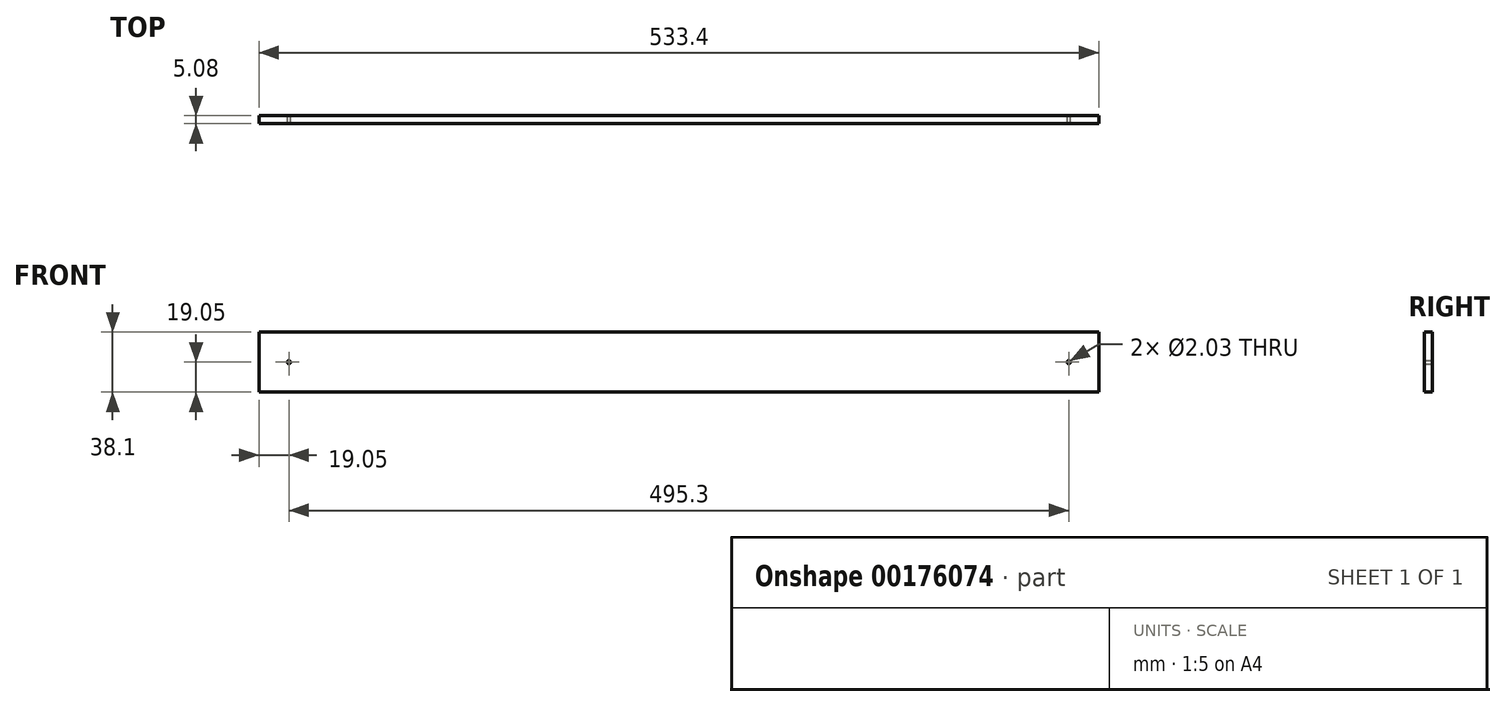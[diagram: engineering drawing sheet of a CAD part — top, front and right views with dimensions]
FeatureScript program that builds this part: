
annotation { "Feature Type Name" : "Feature", "Feature Type Description" : "" }
export const myFeature = defineFeature(function(context is Context, id is Id, definition is map)
    precondition{}
    {
        {
            var Q0;
            Q0=qCreatedBy(makeId("Front.planeOp"),FACE);
            var sketch = newSketch(context, id + "F0", { "sketchPlane" : qUnion([Q0])});
            skLineSegment(sketch, "E0.bottom", {"start": v(0, 0) * mm, "end": v(533.4, 0) * mm});
            skLineSegment(sketch, "E0.top", {"start": v(0, 38.1) * mm, "end": v(533.4, 38.1) * mm});
            skLineSegment(sketch, "E0.left", {"start": v(0, 0) * mm, "end": v(0, 38.1) * mm});
            skLineSegment(sketch, "E0.right", {"start": v(533.4, 0) * mm, "end": v(533.4, 38.1) * mm});
            skCircle(sketch, "E1", {"center": v(19.05, 19.05) * mm, "radius": 1.02 * mm});
            skCircle(sketch, "E2", {"center": v(514.35, 19.05) * mm, "radius": 1.02 * mm});
            skPoint(sketch, "E3", {"position": v(0, 19.05) * mm});
            skSolve(sketch);
        }
        {
            var Q0;
            Q0=makeQuery(id+"F0.imprint","IMPRINT",FACE,{"disambiguationData":[TD([[makeQuery(id+"F0.imprint","IMPRINT",EDGE,{"derivedFrom":sQuery(id+"F0.wireOp",EDGE,"E0.bottom")}),1.0]])]});
            extrude(context, id + "F1", {"entities" : qUnion([Q0]), "depth" : 5.08 * mm});
        }
    });
